# Revit family: Boiler-Weil-McLain-88_Series2_Gas-Oil_Boiler
name_source: partatom
category: Mechanical Equipment
units: mm (PartAtom-declared; Revit-internal decimal feet)

## family parameters
Always vertical = Yes
Cut with Voids When Loaded = No
OmniClass Number = 23.75.10.11.14.11
OmniClass Title = Cast-Iron Boilers
Part Type = Normal
Room Calculation Point = No
Round Connector Dimension = Use Radius
Shared = No
Work Plane-Based = No

## types (1)
- Not a Type - Load Type Catalog
    A = 4' - 7"
    Actual Valve Water Flow = 0 GPM
    Apparent Load = 0 VA
    B = 0' - 0"
    Boiler Horsepower = 59.4
    Boiler Water Pressure Drop = 0.00 psi
    C = 0' - 0"
    Casing = Metal - Weil-McLain - Paint Tan
    D = 1' - 0"
    D Radius = 0' - 6"
    Description = 88 Series 3 Commercial Gas Oil Boiler
    E = 4' - 5 3/4"
    Feet = 9
    Feet Distance = 5' - 2"
    Flue B = No
    Flue C = No
    Frequency = 60 Hz
    Gas Connection Radius = 1"
    Gas Connection Size = 3"
    Gas Net I=B=R = 2382000.0 Btu/h
    Gross I=B=R Rating = 1987000.0 Btu/h
    H = 4' - 7 11/16"
    Height = 5' - 5"
    Length = 5' - 6 3/4"
    Manufacturer = Weil-McLain
    Model = 888
    Net I=B=R Rating = 1728000.0 Btu/h
    Number of Poles = 1
    Phase = 1
    Power Factor = 1
    Product Documentation Link = http://www.weil-mclain.com
    Product Name = 88 Series 3
    Product Page URL = http://www.weil-mclain.com
    Return = 6"
    Return Radius = 3"
    Supply = 5"
    Supply Radius = 3"
    URL = http://www.weil-mclain.com
    Voltage = 230 V
    Width = 3' - 8 1/4"

## geometry (parser evidence)
native form markers: Blend x15, Sweep x19
no freeform markers — native parametric forms only
